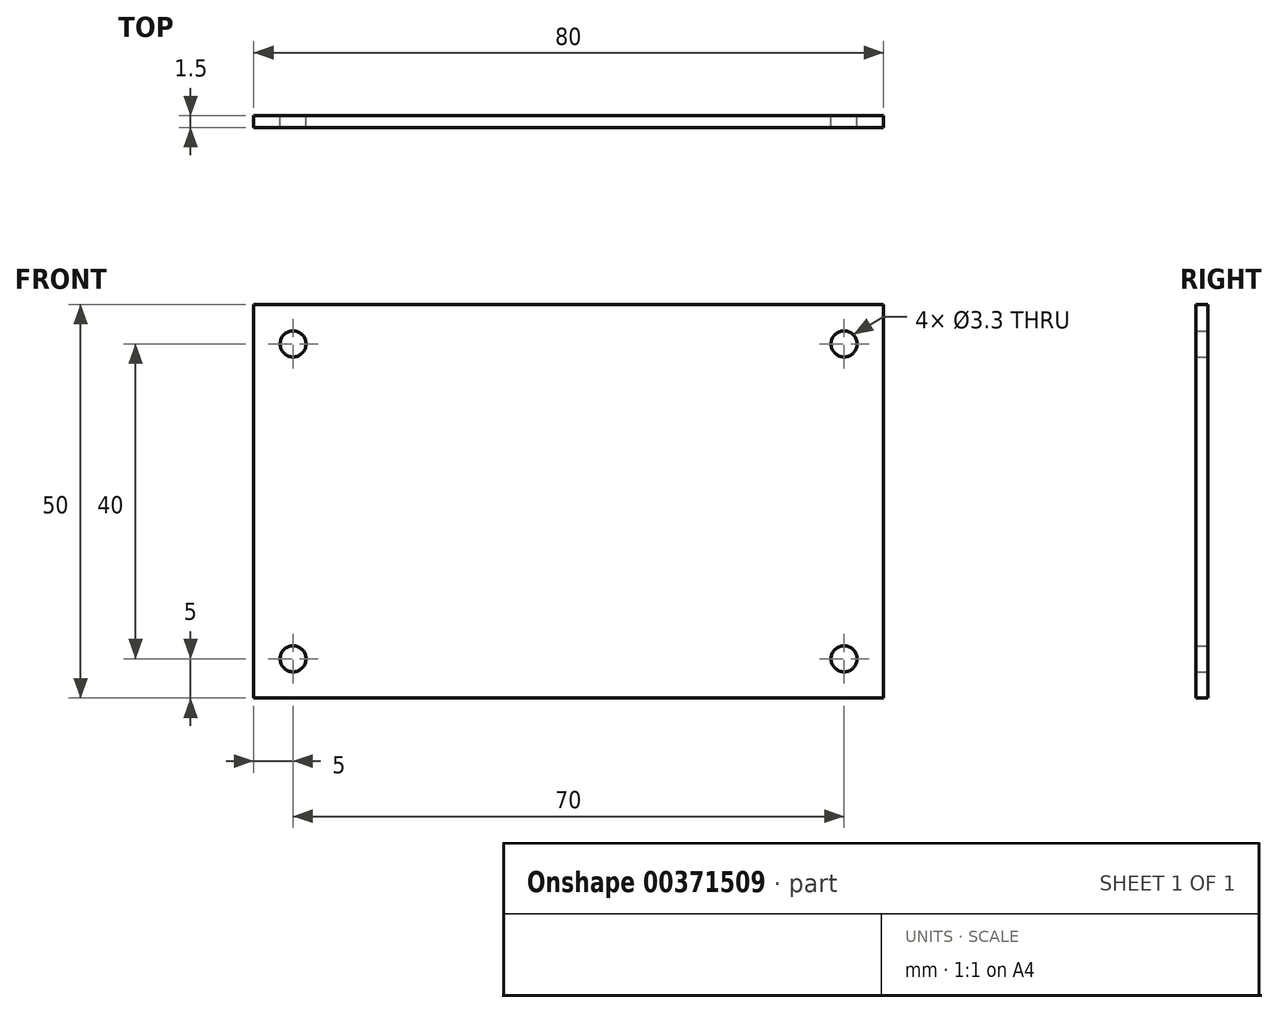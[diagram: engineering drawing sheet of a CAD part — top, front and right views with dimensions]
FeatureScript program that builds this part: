
annotation { "Feature Type Name" : "Feature", "Feature Type Description" : "" }
export const myFeature = defineFeature(function(context is Context, id is Id, definition is map)
    precondition{}
    {
        {
            var Q0;
            Q0=qCreatedBy(makeId("Front.planeOp"),FACE);
            var sketch = newSketch(context, id + "F0", { "sketchPlane" : qUnion([Q0])});
            skLineSegment(sketch, "E0.bottom", {"start": v(-40, 25) * mm, "end": v(40, 25) * mm});
            skLineSegment(sketch, "E0.top", {"start": v(-40, -25) * mm, "end": v(40, -25) * mm});
            skLineSegment(sketch, "E0.left", {"start": v(-40, 25) * mm, "end": v(-40, -25) * mm});
            skLineSegment(sketch, "E0.right", {"start": v(40, 25) * mm, "end": v(40, -25) * mm});
            skPoint(sketch, "E0.middle", {"position": v(0, 0) * mm});
            skCircle(sketch, "E1", {"center": v(-35, 20) * mm, "radius": 1.65 * mm});
            skLineSegment(sketch, "E2", {"start": v(-35, 20) * mm, "end": v(-33.35, 20) * mm, "construction": true});
            skLineSegment(sketch, "E3", {"start": v(35, 20) * mm, "end": v(35, -20) * mm, "construction": true});
            skLineSegment(sketch, "E4", {"start": v(35, -20) * mm, "end": v(-35, -20) * mm, "construction": true});
            skLineSegment(sketch, "E5", {"start": v(-35, -20) * mm, "end": v(-35, 20) * mm, "construction": true});
            skLineSegment(sketch, "E6", {"start": v(-35, 20) * mm, "end": v(35, 20) * mm, "construction": true});
            skCircle(sketch, "E7", {"center": v(35, 20) * mm, "radius": 1.65 * mm});
            skCircle(sketch, "E8", {"center": v(35, -20) * mm, "radius": 1.65 * mm});
            skCircle(sketch, "E9", {"center": v(-35, -20) * mm, "radius": 1.65 * mm});
            skSolve(sketch);
        }
        {
            var Q0;
            Q0=makeQuery(id+"F0.imprint","IMPRINT",FACE,{"disambiguationData":[TD([[makeQuery(id+"F0.imprint","IMPRINT",EDGE,{"derivedFrom":sQuery(id+"F0.wireOp",EDGE,"E0.bottom")}),-1.0]])]});
            extrude(context, id + "F1", {"entities" : qUnion([Q0]), "depth" : 1.5 * mm, "offsetDistance" : 25 * mm});
        }
    });
